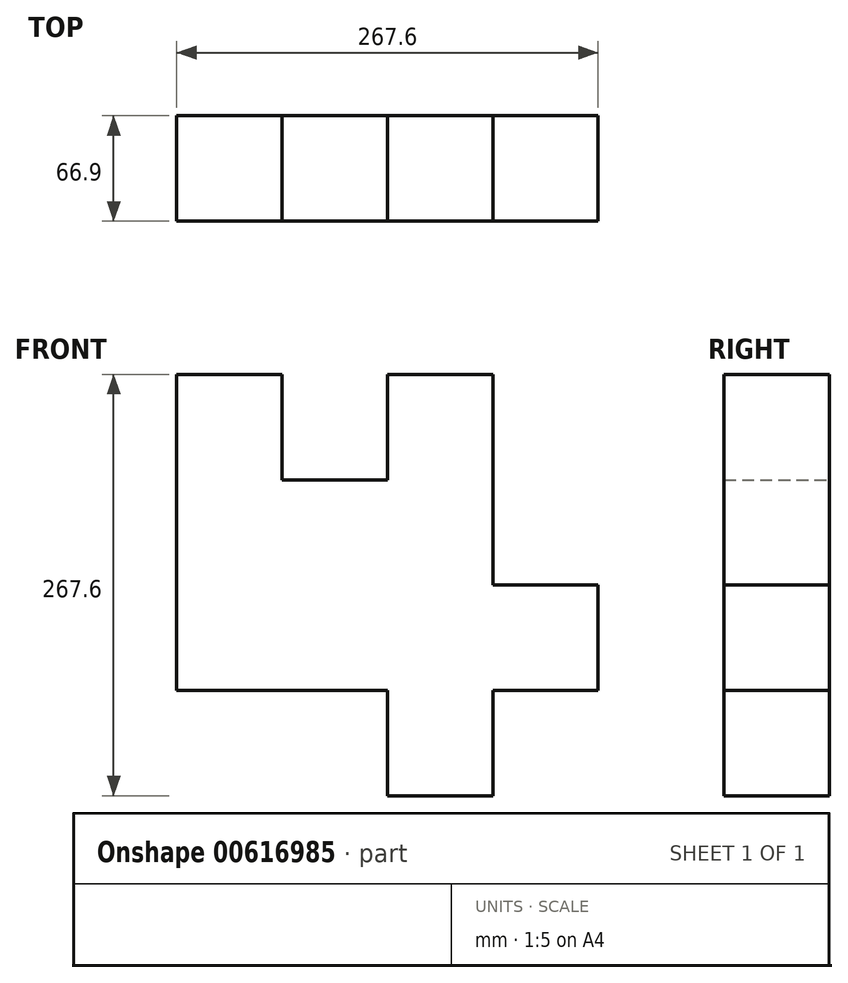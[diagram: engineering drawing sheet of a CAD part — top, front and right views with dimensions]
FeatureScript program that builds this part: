
annotation { "Feature Type Name" : "Feature", "Feature Type Description" : "" }
export const myFeature = defineFeature(function(context is Context, id is Id, definition is map)
    precondition{}
    {
        {
            var Q0;
            Q0=qCreatedBy(makeId("Front.planeOp"),FACE);
            var sketch = newSketch(context, id + "F0", { "sketchPlane" : qUnion([Q0])});
            skLineSegment(sketch, "E0", {"start": v(-166.02, 148.75) * mm, "end": v(-99.12, 148.75) * mm});
            skLineSegment(sketch, "E1", {"start": v(-99.12, 148.75) * mm, "end": v(-99.12, 81.85) * mm});
            skLineSegment(sketch, "E2", {"start": v(-99.12, 81.85) * mm, "end": v(-32.22, 81.85) * mm});
            skLineSegment(sketch, "E3", {"start": v(-32.22, 81.85) * mm, "end": v(-32.22, 148.75) * mm});
            skLineSegment(sketch, "E4", {"start": v(-32.22, 148.75) * mm, "end": v(34.68, 148.75) * mm});
            skLineSegment(sketch, "E5", {"start": v(34.68, 148.75) * mm, "end": v(34.68, 14.95) * mm});
            skLineSegment(sketch, "E6", {"start": v(34.68, 14.95) * mm, "end": v(101.58, 14.95) * mm});
            skLineSegment(sketch, "E7", {"start": v(101.58, 14.95) * mm, "end": v(101.58, -51.95) * mm});
            skLineSegment(sketch, "E8", {"start": v(101.58, -51.95) * mm, "end": v(34.68, -51.95) * mm});
            skLineSegment(sketch, "E9", {"start": v(34.68, -51.95) * mm, "end": v(34.68, -118.85) * mm});
            skLineSegment(sketch, "E10", {"start": v(34.68, -118.85) * mm, "end": v(-32.22, -118.85) * mm});
            skLineSegment(sketch, "E11", {"start": v(-32.22, -118.85) * mm, "end": v(-32.22, -51.95) * mm});
            skLineSegment(sketch, "E12", {"start": v(-32.22, -51.95) * mm, "end": v(-166.02, -51.95) * mm});
            skLineSegment(sketch, "E13", {"start": v(-166.02, 148.75) * mm, "end": v(-166.02, -51.95) * mm});
            skSolve(sketch);
        }
        {
            var Q0;
            Q0 = qSketchRegion(id + "F0", true);
            extrude(context, id + "F1", {"entities" : qUnion([Q0]), "depth" : 66.9 * mm, "offsetDistance" : 25 * mm});
        }
    });
